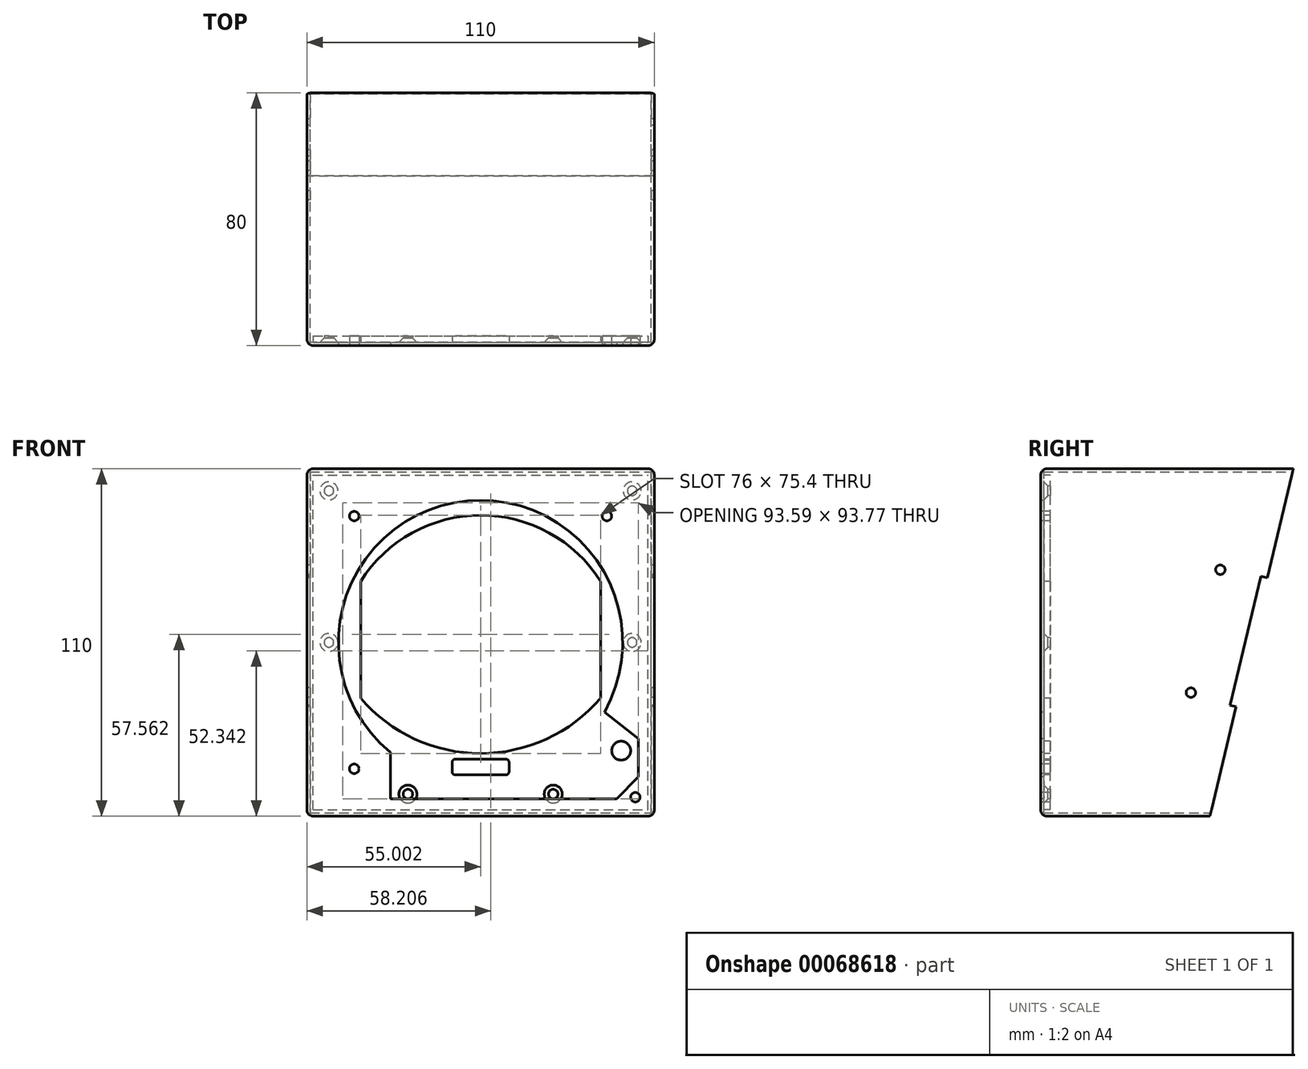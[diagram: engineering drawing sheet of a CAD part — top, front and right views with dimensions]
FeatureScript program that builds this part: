
annotation { "Feature Type Name" : "Feature", "Feature Type Description" : "" }
export const myFeature = defineFeature(function(context is Context, id is Id, definition is map)
    precondition{}
    {
        {
            var Q0;
            Q0=qCreatedBy(makeId("Front.planeOp"),FACE);
            var sketch = newSketch(context, id + "F0", { "sketchPlane" : qUnion([Q0])});
            skLineSegment(sketch, "E0.bottom", {"start": v(-56.84, -55) * mm, "end": v(-166.84, -55) * mm});
            skLineSegment(sketch, "E0.top", {"start": v(-56.84, 55) * mm, "end": v(-166.84, 55) * mm});
            skLineSegment(sketch, "E0.left", {"start": v(-56.84, -55) * mm, "end": v(-56.84, 55) * mm});
            skLineSegment(sketch, "E0.right", {"start": v(-166.84, -55) * mm, "end": v(-166.84, 55) * mm});
            skPoint(sketch, "E0.middle", {"position": v(-111.84, 0) * mm});
            skSolve(sketch);
        }
        {
            var Q0;
            Q0=makeQuery(id+"F0.imprint","IMPRINT",FACE,{"disambiguationData":[TD([[makeQuery(id+"F0.imprint","IMPRINT",EDGE,{"derivedFrom":sQuery(id+"F0.wireOp",EDGE,"E0.bottom")}),-1.0]])]});
            extrude(context, id + "F1", {"entities" : qUnion([Q0]), "endBound" : BoundingType.SYMMETRIC, "depth" : 120 * mm});
        }
        {
            var Q0;
            Q0=makeQuery(id+"F1.opExtrude","CAP_FACE",FACE,{"disambiguationData":[OSD([sQuery(id+"F0.wireOp",EDGE,"E0.bottom"),sQuery(id+"F0.wireOp",EDGE,"E0.top"),sQuery(id+"F0.wireOp",EDGE,"E0.left"),sQuery(id+"F0.wireOp",EDGE,"E0.right")])],"isStart":true});
            shell(context, id + "F2", {"entities" : qUnion([Q0]), "thickness" : 1 * mm});
        }
        {
            var Q0;
            Q0=makeQuery(id+"F1.opExtrude","SWEPT_FACE",FACE,{"disambiguationData":[OSD([sQuery(id+"F0.wireOp",EDGE,"E0.right")])]});
            var sketch = newSketch(context, id + "F3", { "sketchPlane" : qUnion([Q0])});
            skLineSegment(sketch, "E1", {"start": v(-20, 55) * mm, "end": v(6.4, -55) * mm});
            skLineSegment(sketch, "E2", {"start": v(6.4, -55) * mm, "end": v(-89.83, -55) * mm});
            skLineSegment(sketch, "E3", {"start": v(-89.83, -55) * mm, "end": v(-89.83, 55) * mm});
            skLineSegment(sketch, "E4", {"start": v(-89.83, 55) * mm, "end": v(-20, 55) * mm});
            skCircle(sketch, "E5", {"center": v(3.1, 23.01) * mm, "radius": 1.5 * mm});
            skCircle(sketch, "E6", {"center": v(12.44, -15.88) * mm, "radius": 1.5 * mm});
            skLineSegment(sketch, "E7", {"start": v(-6.81, 0.06) * mm, "end": v(32, 9.38) * mm, "construction": true});
            skLineSegment(sketch, "E8", {"start": v(-11.71, 20.48) * mm, "end": v(-1.9, -20.36) * mm});
            skLineSegment(sketch, "E9", {"start": v(-1.9, -20.36) * mm, "end": v(0.04, -19.9) * mm});
            skLineSegment(sketch, "E10", {"start": v(0.04, -19.9) * mm, "end": v(-9.77, 20.95) * mm});
            skLineSegment(sketch, "E11", {"start": v(-9.77, 20.95) * mm, "end": v(-11.71, 20.48) * mm});
            skSolve(sketch);
        }
        {
            var Q0;
            Q0 = qSketchRegion(id + "F3", true);
            extrude(context, id + "F4", {"entities" : qUnion([Q0]), "operationType" : NewBodyOperationType.REMOVE, "oppositeDirection" : true, "depth" : 110 * mm});
        }
        {
            var Q0;
            Q0=makeQuery(id+"F1.opExtrude","CAP_EDGE",EDGE,{"disambiguationData":[OSD([sQuery(id+"F0.wireOp",EDGE,"E0.right")])],"isStart":false});
            var Q1;
            Q1=makeQuery(id+"F1.opExtrude","SWEPT_EDGE",EDGE,{"disambiguationData":[OSD([sQuery(id+"F0.wireOp",EDGE,"E0.top"),sQuery(id+"F0.wireOp",EDGE,"E0.right")])]});
            var Q2;
            Q2=makeQuery(id+"F1.opExtrude","CAP_EDGE",EDGE,{"disambiguationData":[OSD([sQuery(id+"F0.wireOp",EDGE,"E0.top")])],"isStart":false});
            var Q3;
            Q3=makeQuery(id+"F1.opExtrude","CAP_EDGE",EDGE,{"disambiguationData":[OSD([sQuery(id+"F0.wireOp",EDGE,"E0.left")])],"isStart":false});
            var Q4;
            Q4=makeQuery(id+"F1.opExtrude","SWEPT_EDGE",EDGE,{"disambiguationData":[OSD([sQuery(id+"F0.wireOp",EDGE,"E0.top"),sQuery(id+"F0.wireOp",EDGE,"E0.left")])]});
            var Q5;
            Q5=makeQuery(id+"F1.opExtrude","CAP_EDGE",EDGE,{"disambiguationData":[OSD([sQuery(id+"F0.wireOp",EDGE,"E0.bottom")])],"isStart":false});
            var Q6;
            Q6=makeQuery(id+"F1.opExtrude","SWEPT_EDGE",EDGE,{"disambiguationData":[OSD([sQuery(id+"F0.wireOp",EDGE,"E0.bottom"),sQuery(id+"F0.wireOp",EDGE,"E0.left")])]});
            var Q7;
            Q7=makeQuery(id+"F1.opExtrude","SWEPT_EDGE",EDGE,{"disambiguationData":[OSD([sQuery(id+"F0.wireOp",EDGE,"E0.bottom"),sQuery(id+"F0.wireOp",EDGE,"E0.right")])]});
            fillet(context, id + "F5", {"entities" : qUnion([Q0, Q1, Q2, Q3, Q4, Q5, Q6, Q7]), "radius" : 2 * mm, "tangentPropagation" : true, "allowEdgeOverflow" : false});
        }
        {
            var Q0;
            Q0=makeQuery(id+"F1.opExtrude","CAP_FACE",FACE,{"disambiguationData":[OSD([sQuery(id+"F0.wireOp",EDGE,"E0.bottom"),sQuery(id+"F0.wireOp",EDGE,"E0.top"),sQuery(id+"F0.wireOp",EDGE,"E0.left"),sQuery(id+"F0.wireOp",EDGE,"E0.right")])],"isStart":false});
            var sketch = newSketch(context, id + "F6", { "sketchPlane" : qUnion([Q0])});
            skCircle(sketch, "E12", {"center": v(-111.84, 0) * mm, "radius": 45 * mm});
            skLineSegment(sketch, "E13", {"start": v(-140.4, -34.77) * mm, "end": v(-140.4, -49.54) * mm});
            skLineSegment(sketch, "E14", {"start": v(-140.4, -49.54) * mm, "end": v(-68.8, -49.54) * mm});
            skLineSegment(sketch, "E15", {"start": v(-68.8, -49.54) * mm, "end": v(-61.84, -42.48) * mm});
            skLineSegment(sketch, "E16", {"start": v(-61.84, -42.48) * mm, "end": v(-61.84, -30.48) * mm});
            skLineSegment(sketch, "E17", {"start": v(-61.84, -30.48) * mm, "end": v(-72.6, -22.03) * mm});
            skCircle(sketch, "E18", {"center": v(-151.84, 40) * mm, "radius": 1.5 * mm});
            skCircle(sketch, "E19", {"center": v(-71.84, 40) * mm, "radius": 1.5 * mm});
            skCircle(sketch, "E20", {"center": v(-151.84, -40) * mm, "radius": 1.5 * mm});
            skCircle(sketch, "E21", {"center": v(-62.84, -49) * mm, "radius": 1.5 * mm});
            skSolve(sketch);
        }
        {
            var Q0;
            Q0 = qSketchRegion(id + "F6", true);
            extrude(context, id + "F7", {"entities" : qUnion([Q0]), "operationType" : NewBodyOperationType.REMOVE, "oppositeDirection" : true, "depth" : 1 * mm});
        }
        {
            var Q0;
            Q0=makeQuery(id+"F2.opShell","OFFSET_FACE",FACE,{"disambiguationData":[OSD([sQuery(id+"F0.wireOp",EDGE,"E0.bottom"),sQuery(id+"F0.wireOp",EDGE,"E0.top"),sQuery(id+"F0.wireOp",EDGE,"E0.left"),sQuery(id+"F0.wireOp",EDGE,"E0.right")])]});
            var sketch = newSketch(context, id + "F8", { "sketchPlane" : qUnion([Q0])});
            skLineSegment(sketch, "E22.bottom", {"start": v(164.84, -53) * mm, "end": v(58.84, -53) * mm});
            skLineSegment(sketch, "E22.top", {"start": v(164.84, 53) * mm, "end": v(58.84, 53) * mm});
            skLineSegment(sketch, "E22.left", {"start": v(164.84, -53) * mm, "end": v(164.84, 53) * mm});
            skLineSegment(sketch, "E22.right", {"start": v(58.84, -53) * mm, "end": v(58.84, 53) * mm});
            skPoint(sketch, "E22.middle", {"position": v(111.84, 0) * mm});
            skLineSegment(sketch, "E23", {"start": v(73.84, 19.37) * mm, "end": v(73.84, -17.63) * mm});
            skLineSegment(sketch, "E24", {"start": v(149.84, 19.37) * mm, "end": v(149.84, -17.63) * mm});
            skArc(sketch, "E25", {"start": v(149.84, 19.37) * mm, "mid": v(111.84, 40.26) * mm, "end": v(73.84, 19.37) * mm});
            skArc(sketch, "E26", {"start": v(73.84, -17.63) * mm, "mid": v(111.84, -35.14) * mm, "end": v(149.84, -17.63) * mm});
            skLineSegment(sketch, "E27.bottom", {"start": v(103.84, -36.95) * mm, "end": v(119.84, -36.95) * mm});
            skLineSegment(sketch, "E27.top", {"start": v(103.84, -41.95) * mm, "end": v(119.84, -41.95) * mm});
            skLineSegment(sketch, "E27.left", {"start": v(102.84, -37.95) * mm, "end": v(102.84, -40.95) * mm});
            skLineSegment(sketch, "E27.right", {"start": v(120.84, -37.95) * mm, "end": v(120.84, -40.95) * mm});
            skPoint(sketch, "E28.visualSharp", {"position": v(102.84, -36.95) * mm});
            skArc(sketch, "E28.filletArc", {"start": v(103.84, -36.95) * mm, "mid": v(103.13, -37.24) * mm, "end": v(102.84, -37.95) * mm});
            skPoint(sketch, "E29.visualSharp", {"position": v(102.84, -41.95) * mm});
            skArc(sketch, "E29.filletArc", {"start": v(102.84, -40.95) * mm, "mid": v(103.13, -41.65) * mm, "end": v(103.84, -41.95) * mm});
            skPoint(sketch, "E30.visualSharp", {"position": v(120.84, -36.95) * mm});
            skArc(sketch, "E30.filletArc", {"start": v(120.84, -37.95) * mm, "mid": v(120.55, -37.24) * mm, "end": v(119.84, -36.95) * mm});
            skPoint(sketch, "E31.visualSharp", {"position": v(120.84, -41.95) * mm});
            skArc(sketch, "E31.filletArc", {"start": v(119.84, -41.95) * mm, "mid": v(120.55, -41.65) * mm, "end": v(120.84, -40.95) * mm});
            skPoint(sketch, "E32", {"position": v(111.84, -39.45) * mm});
            skCircle(sketch, "E33", {"center": v(151.84, 40) * mm, "radius": 1.5 * mm});
            skCircle(sketch, "E34", {"center": v(71.84, 40) * mm, "radius": 1.5 * mm});
            skCircle(sketch, "E35", {"center": v(62.84, -49) * mm, "radius": 1.5 * mm});
            skCircle(sketch, "E36", {"center": v(151.84, -40) * mm, "radius": 1.5 * mm});
            skCircle(sketch, "E37", {"center": v(67.34, -34.27) * mm, "radius": 3 * mm});
            skSolve(sketch);
        }
        {
            var Q0;
            Q0 = qSketchRegion(id + "F8", true);
            extrude(context, id + "F9", {"entities" : qUnion([Q0]), "depth" : 2 * mm});
        }
        {
            var Q0;
            Q0=makeQuery(id+"F9.opExtrude","CAP_FACE",FACE,{"disambiguationData":[OSD([sQuery(id+"F8.wireOp",EDGE,"E22.bottom"),sQuery(id+"F8.wireOp",EDGE,"E22.top"),sQuery(id+"F8.wireOp",EDGE,"E22.left"),sQuery(id+"F8.wireOp",EDGE,"E22.right"),sQuery(id+"F8.wireOp",EDGE,"E23"),sQuery(id+"F8.wireOp",EDGE,"E24"),sQuery(id+"F8.wireOp",EDGE,"E25"),sQuery(id+"F8.wireOp",EDGE,"E26"),sQuery(id+"F8.wireOp",EDGE,"E27.bottom"),sQuery(id+"F8.wireOp",EDGE,"E27.top"),sQuery(id+"F8.wireOp",EDGE,"E27.left"),sQuery(id+"F8.wireOp",EDGE,"E27.right"),sQuery(id+"F8.wireOp",EDGE,"E28.filletArc"),sQuery(id+"F8.wireOp",EDGE,"E29.filletArc"),sQuery(id+"F8.wireOp",EDGE,"E30.filletArc"),sQuery(id+"F8.wireOp",EDGE,"E31.filletArc"),sQuery(id+"F8.wireOp",EDGE,"E33"),sQuery(id+"F8.wireOp",EDGE,"E34"),sQuery(id+"F8.wireOp",EDGE,"E35"),sQuery(id+"F8.wireOp",EDGE,"E36"),sQuery(id+"F8.wireOp",EDGE,"E37")])],"isStart":true});
            var sketch = newSketch(context, id + "F10", { "sketchPlane" : qUnion([Q0])});
            skLineSegment(sketch, "E38.bottom", {"start": v(-72.84, -43) * mm, "end": v(-150.84, -43) * mm});
            skLineSegment(sketch, "E38.top", {"start": v(-72.84, 43) * mm, "end": v(-150.84, 43) * mm});
            skLineSegment(sketch, "E38.left", {"start": v(-72.84, -43) * mm, "end": v(-72.84, 43) * mm});
            skLineSegment(sketch, "E38.right", {"start": v(-150.84, -43) * mm, "end": v(-150.84, 43) * mm});
            skPoint(sketch, "E38.middle", {"position": v(-111.84, 0) * mm});
            skLineSegment(sketch, "E39.bottom", {"start": v(-56.84, -55) * mm, "end": v(-166.84, -55) * mm});
            skLineSegment(sketch, "E39.top", {"start": v(-56.84, 55) * mm, "end": v(-166.84, 55) * mm});
            skLineSegment(sketch, "E39.left", {"start": v(-56.84, -55) * mm, "end": v(-56.84, 55) * mm});
            skLineSegment(sketch, "E39.right", {"start": v(-166.84, -55) * mm, "end": v(-166.84, 55) * mm});
            skSolve(sketch);
        }
        {
            var Q0;
            {var subQ10=sQuery(id+"F10.wireOp",EDGE,"E38.bottom");Q0=makeQuery(id+"F10.imprint","IMPRINT",FACE,{"disambiguationData":[TD([[makeQuery(id+"F10.imprint","IMPRINT",EDGE,{"derivedFrom":subQ10}),1.0]])]});}
            var sketch = newSketch(context, id + "F11", { "sketchPlane" : qUnion([Q0])});
            skCircle(sketch, "E40", {"center": v(-159.84, 48) * mm, "radius": 1.5 * mm});
            skCircle(sketch, "E41", {"center": v(-63.84, 48) * mm, "radius": 1.5 * mm});
            skCircle(sketch, "E42", {"center": v(-88.84, -48) * mm, "radius": 1.5 * mm});
            skCircle(sketch, "E43", {"center": v(-134.84, -48) * mm, "radius": 1.5 * mm});
            skCircle(sketch, "E44", {"center": v(-159.84, 0) * mm, "radius": 1.5 * mm});
            skCircle(sketch, "E45", {"center": v(-63.84, 0) * mm, "radius": 1.5 * mm});
            skSolve(sketch);
        }
        {
            var Q0;
            Q0=sQuery(id+"F11.wireOp",VERTEX,"E43.center");
            var Q1;
            Q1=sQuery(id+"F11.wireOp",VERTEX,"E42.center");
            var Q2;
            Q2=sQuery(id+"F11.wireOp",VERTEX,"E40.center");
            var Q3;
            Q3=sQuery(id+"F11.wireOp",VERTEX,"E41.center");
            var Q4;
            Q4=sQuery(id+"F11.wireOp",VERTEX,"E44.center");
            var Q5;
            Q5=sQuery(id+"F11.wireOp",VERTEX,"E45.center");
            var Q6;
            Q6=makeQuery(id+"F9.opExtrude","SWEPT_BODY",BODY,{"disambiguationData":[OSD([sQuery(id+"F8.wireOp",EDGE,"E22.bottom"),sQuery(id+"F8.wireOp",EDGE,"E22.top"),sQuery(id+"F8.wireOp",EDGE,"E22.left"),sQuery(id+"F8.wireOp",EDGE,"E22.right"),sQuery(id+"F8.wireOp",EDGE,"E23"),sQuery(id+"F8.wireOp",EDGE,"E24"),sQuery(id+"F8.wireOp",EDGE,"E25"),sQuery(id+"F8.wireOp",EDGE,"E26"),sQuery(id+"F8.wireOp",EDGE,"E27.bottom"),sQuery(id+"F8.wireOp",EDGE,"E27.top"),sQuery(id+"F8.wireOp",EDGE,"E27.left"),sQuery(id+"F8.wireOp",EDGE,"E27.right"),sQuery(id+"F8.wireOp",EDGE,"E28.filletArc"),sQuery(id+"F8.wireOp",EDGE,"E29.filletArc"),sQuery(id+"F8.wireOp",EDGE,"E30.filletArc"),sQuery(id+"F8.wireOp",EDGE,"E31.filletArc"),sQuery(id+"F8.wireOp",EDGE,"E33"),sQuery(id+"F8.wireOp",EDGE,"E34"),sQuery(id+"F8.wireOp",EDGE,"E35"),sQuery(id+"F8.wireOp",EDGE,"E36"),sQuery(id+"F8.wireOp",EDGE,"E37")])]});
            hole(context, id + "F12", {"style" : HoleStyle.C_SINK, "endStyle" : HoleEndStyle.THROUGH, "holeDiameter" : 3 * mm, "cSinkDiameter" : 5.7 * mm, "cSinkAngle" : 90 * degree, "locations" : qUnion([Q0, Q1, Q2, Q3, Q4, Q5]), "scope" : qUnion([Q6]), "isTappedThrough" : true});
        }
    });
